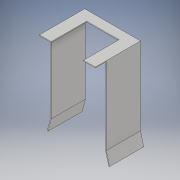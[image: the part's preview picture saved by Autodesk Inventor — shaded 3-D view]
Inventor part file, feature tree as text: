
AUTODESK INVENTOR PART (.ipt)
format: ipt  version: 2019 (Build 230136000, 136)  size: 147,968 bytes
history: native  units: in
note: dims shown in document units (in); Inventor stores cm internally (conversion verified against a paired STEP export)
features: extrude x3, plane x1, sketch x1
ambient origin geometry x8: Origin, YZ Plane, XZ Plane, XY Plane, X Axis, Y Axis, Z Axis, Center Point
bodies: Body1 (feature_tree)
feature tree (5):
  extrude  "Extrusion4"  Depth=0.0625in
  extrude  "Extrusion5"  Depth=6.0341in
  plane  "Work Plane3"
  extrude  "Extrusion7"  Depth=0.0625in
  sketch  "Sketch4"  dims[d1=0.0625in d2=0.0625in d3=6.0341in d4=0.0625in d5=6.0341in d6=0.0625in d13=0.0625in d15=4.2in d28=0.0in d29=75.0deg d30=1.0in d31=2.1in d32=7.0in d33=0.9659in d34=3.5in d35=0.0in d36=2.65in d37=0.0in d42=4.325in d43=2.5in d44=0.9125in d45=0.75in d46=1.0in d47=0.0in]
